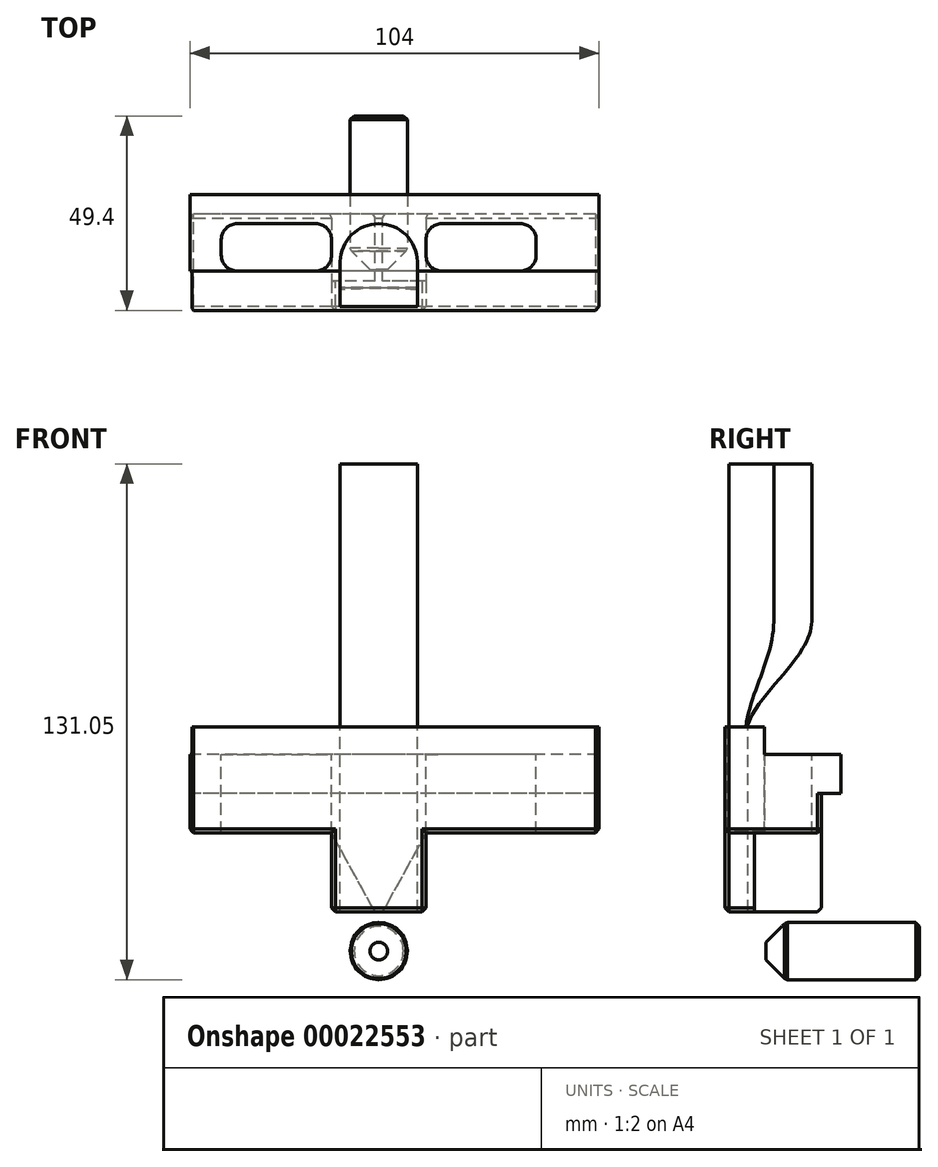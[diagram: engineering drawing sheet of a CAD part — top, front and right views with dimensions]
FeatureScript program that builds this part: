
annotation { "Feature Type Name" : "Feature", "Feature Type Description" : "" }
export const myFeature = defineFeature(function(context is Context, id is Id, definition is map)
    precondition{}
    {
        {
            var Q0;
            Q0=qCreatedBy(makeId("Top.planeOp"),FACE);
            var sketch = newSketch(context, id + "F0", { "sketchPlane" : qUnion([Q0])});
            skLineSegment(sketch, "E0.rect.bottom", {"start": v(9.8, 2) * mm, "end": v(-9.8, 2) * mm});
            skLineSegment(sketch, "E0.rect.top", {"start": v(9.8, -2) * mm, "end": v(-9.8, -2) * mm});
            skLineSegment(sketch, "E0.rect.left", {"start": v(9.8, 2) * mm, "end": v(9.8, -2) * mm});
            skLineSegment(sketch, "E0.rect.right", {"start": v(-9.8, 2) * mm, "end": v(-9.8, -2) * mm});
            skPoint(sketch, "E0.rect.middle", {"position": v(0, 0) * mm});
            skSolve(sketch);
        }
        {
            var Q0;
            Q0=qSketchRegion(id+"F0",true);
            extrude(context, id + "F1", {"entities" : qUnion([Q0]), "depth" : 65 * mm});
        }
        {
            var Q0;
            Q0=makeQuery(id+"F1.opExtrude","SWEPT_FACE",FACE,{"disambiguationData":[OSD([sQuery(id+"F0.wireOp",EDGE,"E0.rect.bottom")])]});
            var sketch = newSketch(context, id + "F2", { "sketchPlane" : qUnion([Q0])});
            skLineSegment(sketch, "E1.rect.bottom", {"start": v(-5, 64.8) * mm, "end": v(5, 64.8) * mm});
            skLineSegment(sketch, "E1.rect.top", {"start": v(-5, 35) * mm, "end": v(5, 35) * mm});
            skLineSegment(sketch, "E1.rect.left", {"start": v(-5, 64.8) * mm, "end": v(-5, 35) * mm});
            skLineSegment(sketch, "E1.rect.right", {"start": v(5, 64.8) * mm, "end": v(5, 35) * mm});
            skPoint(sketch, "E1.rect.middle", {"position": v(0, 49.9) * mm});
            skSolve(sketch);
        }
        {
            var Q0;
            Q0=qSketchRegion(id+"F2",true);
            extrude(context, id + "F3", {"entities" : qUnion([Q0]), "operationType" : NewBodyOperationType.ADD, "depth" : 1 * mm});
        }
        {
            var Q0;
            Q0=makeQuery(id+"F3.opExtrude","SWEPT_EDGE",EDGE,{"disambiguationData":[OSD([sQuery(id+"F2.wireOp",EDGE,"E1.rect.top"),sQuery(id+"F2.wireOp",EDGE,"E1.rect.left")])]});
            var Q1;
            Q1=makeQuery(id+"F3.opExtrude","SWEPT_EDGE",EDGE,{"disambiguationData":[OSD([sQuery(id+"F2.wireOp",EDGE,"E1.rect.top"),sQuery(id+"F2.wireOp",EDGE,"E1.rect.right")])]});
            var Q2;
            Q2=makeQuery(id+"F3.opExtrude","SWEPT_EDGE",EDGE,{"disambiguationData":[OSD([sQuery(id+"F2.wireOp",EDGE,"E1.rect.bottom"),sQuery(id+"F2.wireOp",EDGE,"E1.rect.left")])]});
            var Q3;
            Q3=makeQuery(id+"F3.opExtrude","SWEPT_EDGE",EDGE,{"disambiguationData":[OSD([sQuery(id+"F2.wireOp",EDGE,"E1.rect.bottom"),sQuery(id+"F2.wireOp",EDGE,"E1.rect.right")])]});
            fillet(context, id + "F4", {"entities" : qUnion([Q0, Q1, Q2, Q3]), "radius" : 5 * mm, "tangentPropagation" : true, "allowEdgeOverflow" : false});
        }
        {
            var Q0;
            Q0=makeQuery(id+"F1.opExtrude","CAP_FACE",FACE,{"disambiguationData":[OSD([sQuery(id+"F0.wireOp",EDGE,"E0.rect.bottom"),sQuery(id+"F0.wireOp",EDGE,"E0.rect.top"),sQuery(id+"F0.wireOp",EDGE,"E0.rect.left"),sQuery(id+"F0.wireOp",EDGE,"E0.rect.right")])],"isStart":false});
            cPlane(context, id + "F5", {"entities" : qUnion([Q0]), "cplaneType" : CPlaneType.OFFSET, "offset" : 30 * mm, "width" : 150 * mm, "height" : 150 * mm});
        }
        {
            var Q0;
            Q0=qCreatedBy(id+"F5.planeOp",FACE);
            var sketch = newSketch(context, id + "F6", { "sketchPlane" : qUnion([Q0])});
            skLineSegment(sketch, "E2", {"start": v(9.8, -2) * mm, "end": v(9.8, 9.35) * mm});
            skArc(sketch, "E3", {"start": v(9.8, 9.35) * mm, "mid": v(0, 19) * mm, "end": v(-9.8, 9.35) * mm});
            skLineSegment(sketch, "E4.MirrorCS", {"start": v(-9.8, -2) * mm, "end": v(-9.8, 9.35) * mm});
            skLineSegment(sketch, "E5", {"start": v(-9.8, -2) * mm, "end": v(9.8, -2) * mm});
            skSolve(sketch);
        }
        {
            var Q1;
            Q1=makeQuery(id+"F1.opExtrude","CAP_FACE",FACE,{"disambiguationData":[OSD([sQuery(id+"F0.wireOp",EDGE,"E0.rect.bottom"),sQuery(id+"F0.wireOp",EDGE,"E0.rect.top"),sQuery(id+"F0.wireOp",EDGE,"E0.rect.left"),sQuery(id+"F0.wireOp",EDGE,"E0.rect.right")])],"isStart":false});
            var Q2;
            Q2=makeQuery(id+"F6.imprint","IMPRINT",FACE,{"disambiguationData":[TD([[makeQuery(id+"F6.imprint","IMPRINT",EDGE,{"derivedFrom":sQuery(id+"F6.wireOp",EDGE,"E2")}),1.0]])]});
            loft(context, id + "F7", {"operationType" : NewBodyOperationType.ADD, "startCondition" : LoftEndDerivativeType.NORMAL_TO_PROFILE, "startMagnitude" : 1, "endCondition" : LoftEndDerivativeType.NORMAL_TO_PROFILE, "endMagnitude" : 1, "sheetProfilesArray" : [{ "sheetProfileEntities" : qUnion([Q1]) }, { "sheetProfileEntities" : qUnion([Q2]) }]});
        }
        {
            var Q0;
            Q0=makeQuery(id+"F7.opLoft","CAP_FACE",FACE,{"disambiguationData":[OSD([makeQuery(id+"F6.imprint","IMPRINT",FACE,{"disambiguationData":[TD([[makeQuery(id+"F6.imprint","IMPRINT",EDGE,{"derivedFrom":sQuery(id+"F6.wireOp",EDGE,"E2")}),1.0]])]})])],"isStart":true});
            extrude(context, id + "F8", {"entities" : qUnion([Q0]), "operationType" : NewBodyOperationType.ADD, "depth" : 40 * mm});
        }
        {
            var Q0;
            Q0=qCreatedBy(makeId("Top.planeOp"),FACE);
            cPlane(context, id + "F9", {"entities" : qUnion([Q0]), "cplaneType" : CPlaneType.OFFSET, "offset" : 11.2 * mm, "width" : 150 * mm, "height" : 150 * mm});
        }
        {
            var Q0;
            Q0=qCreatedBy(id+"F9.planeOp",FACE);
            cPlane(context, id + "F10", {"entities" : qUnion([Q0]), "cplaneType" : CPlaneType.OFFSET, "offset" : 40 * mm, "width" : 150 * mm, "height" : 150 * mm});
        }
        {
            var Q0;
            Q0=qCreatedBy(makeId("Right.planeOp"),FACE);
            var sketch = newSketch(context, id + "F11", { "sketchPlane" : qUnion([Q0])});
            skLineSegment(sketch, "E6", {"start": v(-3, 68.2) * mm, "end": v(-3, 41.2) * mm});
            skLineSegment(sketch, "E7", {"start": v(-3, 41.2) * mm, "end": v(21.4, 41.2) * mm});
            skLineSegment(sketch, "E8", {"start": v(21.4, 41.2) * mm, "end": v(21.4, 51.2) * mm});
            skLineSegment(sketch, "E9", {"start": v(21.4, 51.2) * mm, "end": v(26.4, 51.2) * mm});
            skLineSegment(sketch, "E10", {"start": v(26.4, 51.2) * mm, "end": v(26.4, 61.2) * mm});
            skLineSegment(sketch, "E11", {"start": v(26.4, 61.2) * mm, "end": v(7, 61.2) * mm});
            skLineSegment(sketch, "E12", {"start": v(7, 61.2) * mm, "end": v(7, 68.2) * mm});
            skLineSegment(sketch, "E13", {"start": v(7, 68.2) * mm, "end": v(-3, 68.2) * mm});
            skSolve(sketch);
        }
        {
            var Q0;
            Q0 = qSketchRegion(id + "F11", true);
            extrude(context, id + "F12", {"entities" : qUnion([Q0]), "depth" : (104 - 48) * mm, "hasSecondDirection" : true, "secondDirectionOppositeDirection" : true, "secondDirectionDepth" : 48 * mm});
        }
        {
            var Q0;
            Q0=makeQuery(id+"F12.opExtrude","SWEPT_FACE",FACE,{"disambiguationData":[OSD([sQuery(id+"F11.wireOp",EDGE,"E7")])]});
            var sketch = newSketch(context, id + "F13", { "sketchPlane" : qUnion([Q0])});
            skLineSegment(sketch, "E14", {"start": v(0, -21.4) * mm, "end": v(0, 3) * mm});
            skLineSegment(sketch, "E15.rect.bottom", {"start": v(-12, -21.4) * mm, "end": v(12, -21.4) * mm});
            skLineSegment(sketch, "E15.rect.top", {"start": v(-12, 3) * mm, "end": v(12, 3) * mm});
            skLineSegment(sketch, "E15.rect.left", {"start": v(-12, -21.4) * mm, "end": v(-12, 3) * mm});
            skLineSegment(sketch, "E15.rect.right", {"start": v(12, -21.4) * mm, "end": v(12, 3) * mm});
            skPoint(sketch, "E15.rect.middle", {"position": v(0, -9.2) * mm});
            skSolve(sketch);
        }
        {
            var Q0;
            Q0 = qSketchRegion(id + "F13", true);
            extrude(context, id + "F14", {"entities" : qUnion([Q0]), "operationType" : NewBodyOperationType.ADD, "depth" : 20 * mm});
        }
        {
            var Q0;
            Q0=makeQuery(id+"F12.opExtrude","SWEPT_FACE",FACE,{"disambiguationData":[OSD([sQuery(id+"F11.wireOp",EDGE,"E11")])]});
            var sketch = newSketch(context, id + "F15", { "sketchPlane" : qUnion([Q0])});
            skLineSegment(sketch, "E16.rect.bottom", {"start": v(-36, 19) * mm, "end": v(-16, 19) * mm});
            skLineSegment(sketch, "E16.rect.top", {"start": v(-36, 7) * mm, "end": v(-16, 7) * mm});
            skLineSegment(sketch, "E16.rect.left", {"start": v(-40, 15) * mm, "end": v(-40, 11) * mm});
            skLineSegment(sketch, "E16.rect.right", {"start": v(-12, 15) * mm, "end": v(-12, 11) * mm});
            skPoint(sketch, "E16.rect.middle", {"position": v(-26, 13) * mm});
            skPoint(sketch, "E17.visualSharp", {"position": v(-40, 19) * mm});
            skArc(sketch, "E17.filletArc", {"start": v(-36, 19) * mm, "mid": v(-38.83, 17.83) * mm, "end": v(-40, 15) * mm});
            skPoint(sketch, "E18.visualSharp", {"position": v(-12, 19) * mm});
            skArc(sketch, "E18.filletArc", {"start": v(-12, 15) * mm, "mid": v(-13.17, 17.83) * mm, "end": v(-16, 19) * mm});
            skPoint(sketch, "E19.visualSharp", {"position": v(-12, 7) * mm});
            skArc(sketch, "E19.filletArc", {"start": v(-16, 7) * mm, "mid": v(-13.17, 8.17) * mm, "end": v(-12, 11) * mm});
            skPoint(sketch, "E20.visualSharp", {"position": v(-40, 7) * mm});
            skArc(sketch, "E20.filletArc", {"start": v(-40, 11) * mm, "mid": v(-38.83, 8.17) * mm, "end": v(-36, 7) * mm});
            skLineSegment(sketch, "E21.MirrorCS", {"start": v(40, 15) * mm, "end": v(40, 11) * mm});
            skPoint(sketch, "E22.MirrorP", {"position": v(12, 7) * mm});
            skArc(sketch, "E23.MirrorCS", {"start": v(16, 7) * mm, "mid": v(13.17, 8.17) * mm, "end": v(12, 11) * mm});
            skLineSegment(sketch, "E24.MirrorCS", {"start": v(12, 15) * mm, "end": v(12, 11) * mm});
            skPoint(sketch, "E25.MirrorP", {"position": v(26, 13) * mm});
            skPoint(sketch, "E26.MirrorP", {"position": v(40, 19) * mm});
            skLineSegment(sketch, "E27.MirrorCS", {"start": v(36, 19) * mm, "end": v(16, 19) * mm});
            skPoint(sketch, "E28.MirrorP", {"position": v(40, 7) * mm});
            skPoint(sketch, "E29.MirrorP", {"position": v(12, 19) * mm});
            skArc(sketch, "E30.MirrorCS", {"start": v(40, 11) * mm, "mid": v(38.83, 8.17) * mm, "end": v(36, 7) * mm});
            skArc(sketch, "E31.MirrorCS", {"start": v(36, 19) * mm, "mid": v(38.83, 17.83) * mm, "end": v(40, 15) * mm});
            skArc(sketch, "E32.MirrorCS", {"start": v(12, 15) * mm, "mid": v(13.17, 17.83) * mm, "end": v(16, 19) * mm});
            skLineSegment(sketch, "E33.MirrorCS", {"start": v(36, 7) * mm, "end": v(16, 7) * mm});
            skSolve(sketch);
        }
        {
            var Q0;
            Q0 = qSketchRegion(id + "F15", true);
            extrude(context, id + "F16", {"entities" : qUnion([Q0]), "operationType" : NewBodyOperationType.REMOVE, "oppositeDirection" : true, "depth" : 25 * mm});
        }
        {
            var Q0;
            Q0=makeQuery(id+"F2.imprint","IMPRINT",FACE,{"disambiguationData":[TD([[makeQuery(id+"F2.imprint","IMPRINT",EDGE,{"derivedFrom":sQuery(id+"F2.wireOp",EDGE,"E1.rect.bottom")}),1.0]])]});
            var sketch = newSketch(context, id + "F17", { "sketchPlane" : qUnion([Q0])});
            skLineSegment(sketch, "E34.rect.bottom", {"start": v(-5, 6.2) * mm, "end": v(5, 6.2) * mm});
            skLineSegment(sketch, "E34.rect.top", {"start": v(-5, 16.2) * mm, "end": v(5, 16.2) * mm});
            skLineSegment(sketch, "E34.rect.left", {"start": v(-5, 6.2) * mm, "end": v(-5, 16.2) * mm});
            skLineSegment(sketch, "E34.rect.right", {"start": v(5, 6.2) * mm, "end": v(5, 16.2) * mm});
            skPoint(sketch, "E34.rect.middle", {"position": v(0, 11.2) * mm});
            skSolve(sketch);
        }
        {
            var Q0;
            Q0 = qSketchRegion(id + "F17", true);
            extrude(context, id + "F18", {"entities" : qUnion([Q0]), "operationType" : NewBodyOperationType.REMOVE, "oppositeDirection" : true, "depth" : .6 * mm});
        }
        {
            var Q0;
            Q0=makeQuery(id+"F14.boolean.opBoolean","MERGE",FACE,{"derivedFrom":[makeQuery(id+"F12.opExtrude","SWEPT_FACE",FACE,{"disambiguationData":[OSD([sQuery(id+"F11.wireOp",EDGE,"E8")])]}),makeQuery(id+"F14.opExtrude","SWEPT_FACE",FACE,{"disambiguationData":[OSD([sQuery(id+"F13.wireOp",EDGE,"E15.rect.bottom")])]})]});
            var sketch = newSketch(context, id + "F19", { "sketchPlane" : qUnion([Q0])});
            skCircle(sketch, "E35", {"center": v(0, 11.2) * mm, "radius": 7.25 * mm});
            skSolve(sketch);
        }
        {
            var Q0;
            Q0 = qSketchRegion(id + "F19", true);
            extrude(context, id + "F20", {"entities" : qUnion([Q0]), "operationType" : NewBodyOperationType.ADD, "depth" : 25 * mm, "hasSecondDirection" : true, "secondDirectionOppositeDirection" : true, "secondDirectionDepth" : (25.4 - 11.4) * mm});
        }
        {
            var Q0;
            Q0=makeQuery(id+"F20.opExtrude","CAP_EDGE",EDGE,{"disambiguationData":[OSD([sQuery(id+"F19.wireOp",EDGE,"E35")])],"isStart":true});
            chamfer(context, id + "F21", {"entities" : qUnion([Q0]), "width" : 5 * mm, "tangentPropagation" : true});
        }
        {
            var Q0;
            Q0=makeQuery(id+"F12.opExtrude","SWEPT_FACE",FACE,{"disambiguationData":[OSD([sQuery(id+"F11.wireOp",EDGE,"E13")])]});
            var sketch = newSketch(context, id + "F22", { "sketchPlane" : qUnion([Q0])});
            skLineSegment(sketch, "E36.rect.bottom", {"start": v(9.9, -2) * mm, "end": v(-9.9, -2) * mm});
            skLineSegment(sketch, "E36.rect.top", {"start": v(9.9, 2.8) * mm, "end": v(-9.9, 2.8) * mm});
            skLineSegment(sketch, "E36.rect.left", {"start": v(9.9, -2) * mm, "end": v(9.9, 2.8) * mm});
            skLineSegment(sketch, "E36.rect.right", {"start": v(-9.9, -2) * mm, "end": v(-9.9, 2.8) * mm});
            skPoint(sketch, "E36.rect.middle", {"position": v(0, 0.4) * mm});
            skSolve(sketch);
        }
        {
            var Q0;
            Q0 = qSketchRegion(id + "F22", true);
            extrude(context, id + "F23", {"entities" : qUnion([Q0]), "operationType" : NewBodyOperationType.REMOVE, "endBound" : BoundingType.THROUGH_ALL, "oppositeDirection" : true, "depth" : 25 * mm});
        }
        {
            var Q0;
            Q0=makeQuery(id+"F14.boolean.opBoolean","MERGE",FACE,{"derivedFrom":[makeQuery(id+"F12.opExtrude","SWEPT_FACE",FACE,{"disambiguationData":[OSD([sQuery(id+"F11.wireOp",EDGE,"E8")])]}),makeQuery(id+"F14.opExtrude","SWEPT_FACE",FACE,{"disambiguationData":[OSD([sQuery(id+"F13.wireOp",EDGE,"E15.rect.bottom")])]})]});
            var sketch = newSketch(context, id + "F24", { "sketchPlane" : qUnion([Q0])});
            skLineSegment(sketch, "E37", {"start": v(-12, 41.2) * mm, "end": v(-1, 21.2) * mm});
            skLineSegment(sketch, "E38", {"start": v(1, 21.2) * mm, "end": v(12, 41.2) * mm});
            skLineSegment(sketch, "E39", {"start": v(-12, 41.2) * mm, "end": v(-12, 21.2) * mm});
            skLineSegment(sketch, "E40", {"start": v(12, 21.2) * mm, "end": v(12, 41.2) * mm});
            skLineSegment(sketch, "E41", {"start": v(-12, 21.2) * mm, "end": v(-1, 21.2) * mm});
            skLineSegment(sketch, "E42", {"start": v(1, 21.2) * mm, "end": v(12, 21.2) * mm});
            skSolve(sketch);
        }
        {
            var Q0;
            Q0 = qSketchRegion(id + "F24", true);
            extrude(context, id + "F25", {"entities" : qUnion([Q0]), "operationType" : NewBodyOperationType.REMOVE, "oppositeDirection" : true, "depth" : 17 * mm});
        }
        {
            var Q0;
            {var subQ0=sQuery(id+"F11.wireOp",EDGE,"E7");var subQ1=sQuery(id+"F11.wireOp",EDGE,"E8");Q0=makeQuery(id+"F14.boolean.opBoolean","SPLIT",EDGE,{"disambiguationData":[TD([makeQuery(id+"F14.opExtrude","SWEPT_FACE",FACE,{"disambiguationData":[OSD([sQuery(id+"F13.wireOp",EDGE,"E15.rect.right")])]})])],"derivedFrom":makeQuery(id+"F12.opExtrude","SWEPT_EDGE",EDGE,{"disambiguationData":[OSD([subQ0,subQ1])]})});}
            var Q1;
            Q1=makeQuery(id+"F12.opExtrude","CAP_EDGE",EDGE,{"disambiguationData":[OSD([sQuery(id+"F11.wireOp",EDGE,"E7")])],"isStart":false});
            var Q2;
            {var subQ0=sQuery(id+"F11.wireOp",EDGE,"E6");var subQ1=sQuery(id+"F11.wireOp",EDGE,"E7");Q2=makeQuery(id+"F14.boolean.opBoolean","SPLIT",EDGE,{"disambiguationData":[TD([makeQuery(id+"F14.opExtrude","SWEPT_FACE",FACE,{"disambiguationData":[OSD([sQuery(id+"F13.wireOp",EDGE,"E15.rect.right")])]})])],"derivedFrom":makeQuery(id+"F12.opExtrude","SWEPT_EDGE",EDGE,{"disambiguationData":[OSD([subQ0,subQ1])]})});}
            var Q3;
            Q3=makeQuery(id+"F25.boolean.opBoolean","COPY",EDGE,{"derivedFrom":makeQuery(id+"F25.opExtrude","CAP_EDGE",EDGE,{"disambiguationData":[OSD([sQuery(id+"F24.wireOp",EDGE,"E37")])],"isStart":true})});
            var Q4;
            Q4=makeQuery(id+"F14.opExtrude","SWEPT_EDGE",EDGE,{"disambiguationData":[OSD([sQuery(id+"F11.wireOp",EDGE,"E6"),sQuery(id+"F11.wireOp",EDGE,"E7"),sQuery(id+"F13.wireOp",EDGE,"E15.rect.top"),sQuery(id+"F13.wireOp",EDGE,"E15.rect.right")])]});
            var Q5;
            Q5=makeQuery(id+"F25.boolean.opBoolean","COPY",EDGE,{"derivedFrom":makeQuery(id+"F25.opExtrude","CAP_EDGE",EDGE,{"disambiguationData":[OSD([sQuery(id+"F24.wireOp",EDGE,"E39")])],"isStart":false})});
            var Q6;
            Q6=makeQuery(id+"F25.boolean.opBoolean","COPY",EDGE,{"derivedFrom":makeQuery(id+"F25.opExtrude","CAP_EDGE",EDGE,{"disambiguationData":[OSD([sQuery(id+"F24.wireOp",EDGE,"E41")])],"isStart":false})});
            var Q7;
            Q7=makeQuery(id+"F14.opExtrude","CAP_EDGE",EDGE,{"disambiguationData":[OSD([sQuery(id+"F13.wireOp",EDGE,"E15.rect.right")])],"isStart":false});
            var Q8;
            Q8=makeQuery(id+"F14.opExtrude","CAP_EDGE",EDGE,{"disambiguationData":[OSD([sQuery(id+"F13.wireOp",EDGE,"E15.rect.top")])],"isStart":false});
            var Q9;
            Q9=makeQuery(id+"F25.boolean.opBoolean","COPY",EDGE,{"derivedFrom":makeQuery(id+"F25.opExtrude","CAP_EDGE",EDGE,{"disambiguationData":[OSD([sQuery(id+"F24.wireOp",EDGE,"E38")])],"isStart":true})});
            var Q10;
            Q10=makeQuery(id+"F14.opExtrude","CAP_EDGE",EDGE,{"disambiguationData":[OSD([sQuery(id+"F13.wireOp",EDGE,"E15.rect.bottom")])],"isStart":false});
            var Q11;
            {var subQ0=sQuery(id+"F11.wireOp",EDGE,"E7");var subQ1=sQuery(id+"F11.wireOp",EDGE,"E8");Q11=makeQuery(id+"F14.boolean.opBoolean","SPLIT",EDGE,{"disambiguationData":[TD([makeQuery(id+"F14.opExtrude","SWEPT_FACE",FACE,{"disambiguationData":[OSD([sQuery(id+"F13.wireOp",EDGE,"E15.rect.left")])]})])],"derivedFrom":makeQuery(id+"F12.opExtrude","SWEPT_EDGE",EDGE,{"disambiguationData":[OSD([subQ0,subQ1])]})});}
            var Q12;
            Q12=makeQuery(id+"F12.opExtrude","CAP_EDGE",EDGE,{"disambiguationData":[OSD([sQuery(id+"F11.wireOp",EDGE,"E7")])],"isStart":true});
            var Q13;
            {var subQ0=sQuery(id+"F11.wireOp",EDGE,"E6");var subQ1=sQuery(id+"F11.wireOp",EDGE,"E7");Q13=makeQuery(id+"F14.boolean.opBoolean","SPLIT",EDGE,{"disambiguationData":[TD([makeQuery(id+"F14.opExtrude","SWEPT_FACE",FACE,{"disambiguationData":[OSD([sQuery(id+"F13.wireOp",EDGE,"E15.rect.left")])]})])],"derivedFrom":makeQuery(id+"F12.opExtrude","SWEPT_EDGE",EDGE,{"disambiguationData":[OSD([subQ0,subQ1])]})});}
            var Q14;
            Q14=makeQuery(id+"F20.opExtrude","SWEPT_FACE",FACE,{"disambiguationData":[OSD([sQuery(id+"F19.wireOp",EDGE,"E35")])]});
            var Q15;
            Q15=makeQuery(id+"F25.boolean.opBoolean","COPY",EDGE,{"derivedFrom":makeQuery(id+"F25.opExtrude","CAP_EDGE",EDGE,{"disambiguationData":[OSD([sQuery(id+"F24.wireOp",EDGE,"E42")])],"isStart":false})});
            var Q16;
            Q16=makeQuery(id+"F14.opExtrude","CAP_EDGE",EDGE,{"disambiguationData":[OSD([sQuery(id+"F13.wireOp",EDGE,"E15.rect.left")])],"isStart":false});
            var Q17;
            Q17=makeQuery(id+"F12.opExtrude","CAP_EDGE",EDGE,{"disambiguationData":[OSD([sQuery(id+"F11.wireOp",EDGE,"E6")])],"isStart":true});
            var Q18;
            Q18=makeQuery(id+"F12.opExtrude","CAP_EDGE",EDGE,{"disambiguationData":[OSD([sQuery(id+"F11.wireOp",EDGE,"E8")])],"isStart":true});
            var Q19;
            Q19=makeQuery(id+"F12.opExtrude","CAP_EDGE",EDGE,{"disambiguationData":[OSD([sQuery(id+"F11.wireOp",EDGE,"E8")])],"isStart":false});
            var Q20;
            Q20=makeQuery(id+"F12.opExtrude","CAP_EDGE",EDGE,{"disambiguationData":[OSD([sQuery(id+"F11.wireOp",EDGE,"E6")])],"isStart":false});
            var Q21;
            Q21=makeQuery(id+"F14.opExtrude","SWEPT_EDGE",EDGE,{"disambiguationData":[OSD([sQuery(id+"F11.wireOp",EDGE,"E6"),sQuery(id+"F11.wireOp",EDGE,"E7"),sQuery(id+"F13.wireOp",EDGE,"E15.rect.top"),sQuery(id+"F13.wireOp",EDGE,"E15.rect.left")])]});
            var Q22;
            Q22=makeQuery(id+"F25.boolean.opBoolean","COPY",EDGE,{"derivedFrom":makeQuery(id+"F25.opExtrude","CAP_EDGE",EDGE,{"disambiguationData":[OSD([sQuery(id+"F24.wireOp",EDGE,"E40")])],"isStart":false})});
            chamfer(context, id + "F26", {"entities" : qUnion([Q0, Q1, Q2, Q3, Q4, Q5, Q6, Q7, Q8, Q9, Q10, Q11, Q12, Q13, Q14, Q15, Q16, Q17, Q18, Q19, Q20, Q21, Q22]), "width" : 1 * mm, "tangentPropagation" : true});
        }
        {
            var Q0;
            Q0=makeQuery(id+"F12.opExtrude","CAP_FACE",FACE,{"disambiguationData":[OSD([sQuery(id+"F11.wireOp",EDGE,"E6"),sQuery(id+"F11.wireOp",EDGE,"E7"),sQuery(id+"F11.wireOp",EDGE,"E8"),sQuery(id+"F11.wireOp",EDGE,"E9"),sQuery(id+"F11.wireOp",EDGE,"E10"),sQuery(id+"F11.wireOp",EDGE,"E11"),sQuery(id+"F11.wireOp",EDGE,"E12"),sQuery(id+"F11.wireOp",EDGE,"E13")])],"isStart":true});
            var sketch = newSketch(context, id + "F27", { "sketchPlane" : qUnion([Q0])});
            skLineSegment(sketch, "E43.bottom", {"start": v(-7, 68.2) * mm, "end": v(3.2, 68.2) * mm});
            skLineSegment(sketch, "E43.top", {"start": v(-7, 41.44) * mm, "end": v(3.2, 41.44) * mm});
            skLineSegment(sketch, "E43.left", {"start": v(-7, 68.2) * mm, "end": v(-7, 41.44) * mm});
            skLineSegment(sketch, "E43.right", {"start": v(3.2, 68.2) * mm, "end": v(3.2, 41.44) * mm});
            skSolve(sketch);
        }
        {
            var Q0;
            Q0 = qSketchRegion(id + "F27", true);
            extrude(context, id + "F28", {"entities" : qUnion([Q0]), "operationType" : NewBodyOperationType.REMOVE, "oppositeDirection" : true, "depth" : .6 * mm});
        }
    });
